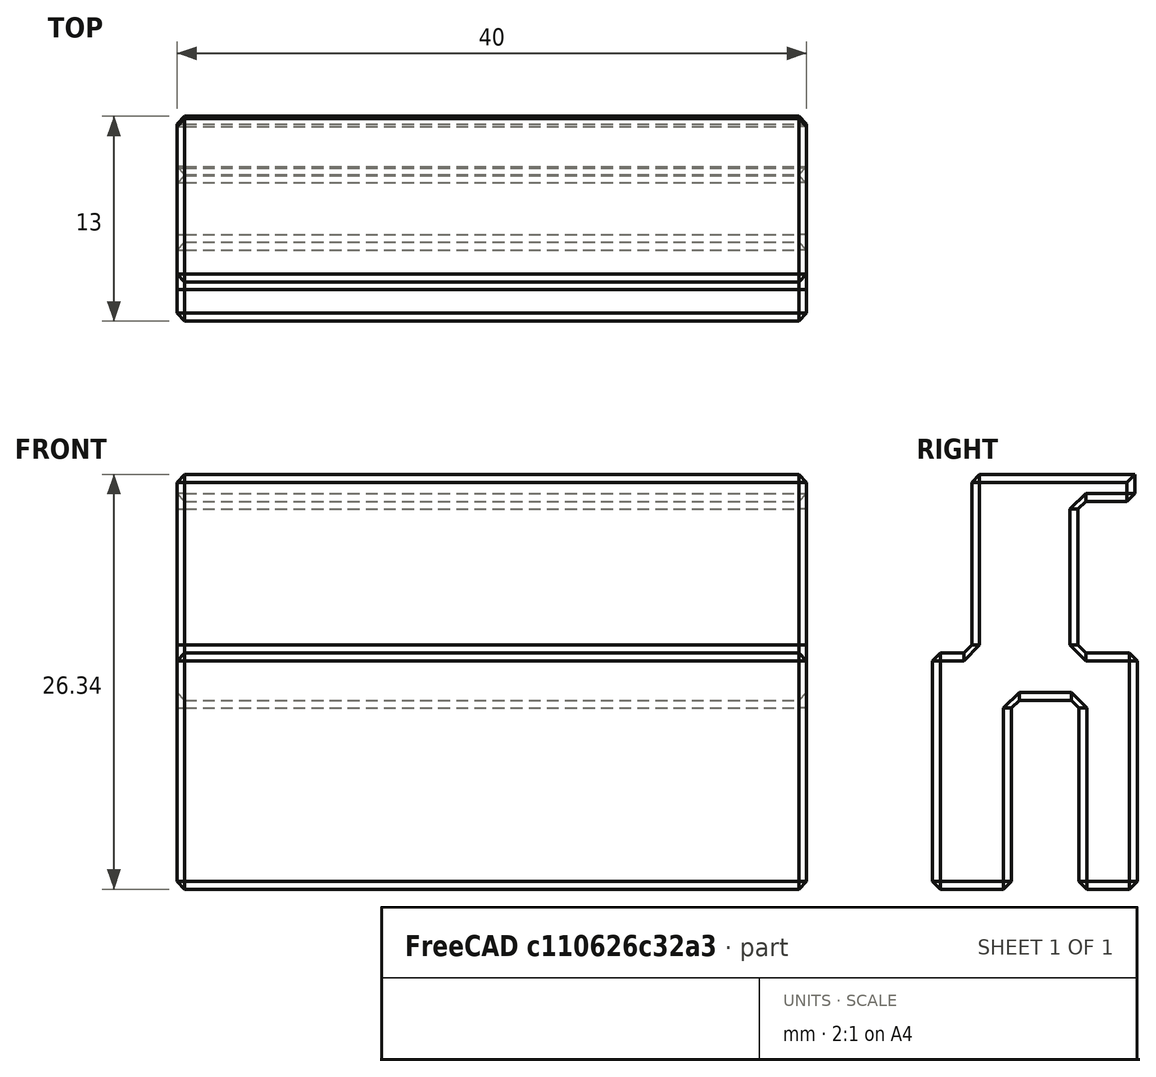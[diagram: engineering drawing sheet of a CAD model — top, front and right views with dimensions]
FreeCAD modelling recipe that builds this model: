
FCSTD DOCUMENT  (FreeCAD 0.21R)
Label: sensor_holder_adapter2
License: All rights reserved
LicenseURL: http://en.wikipedia.org/wiki/All_rights_reserved
objects: Sketcher::SketchObject×1, PartDesign::Pad×1, Mesh::Feature×1, PartDesign::Chamfer×1, PartDesign::Body×1
note: 6 computed .brp shape members not serialized (recipe doc carries the construction recipe); baked Part::Feature solids carry a one-line shape summary decoded from their .brp

FEATURE [Sketcher::SketchObject] Sketch005
  FullyConstrained = false
  MapMode = 5
  Placement = pos=(0,0,0) rot=(0.57735,0.57735,0.57735;2.0944rad)
  sketch-geometry (15):
    g0: LineSegment StartX=4.3 StartY=-10 StartZ=0 EndX=8 EndY=-10 EndZ=0
    g1: LineSegment StartX=8 StartY=-10 StartZ=0 EndX=8 EndY=5 EndZ=0
    g2: LineSegment StartX=4.3 StartY=2 StartZ=0 EndX=4.3 EndY=-10 EndZ=0
    g3: LineSegment StartX=0 StartY=2 StartZ=0 EndX=4.3 EndY=2 EndZ=0
    g4: LineSegment StartX=-5 StartY=5 StartZ=0 EndX=-2.51766 EndY=5 EndZ=0
    g5: LineSegment StartX=-5 StartY=5 StartZ=0 EndX=-5 EndY=-2.48828 EndZ=0
    g6: LineSegment StartX=-5 StartY=-2.48828 StartZ=0 EndX=-5 EndY=-10 EndZ=0
    g7: LineSegment StartX=-5 StartY=-10 StartZ=0 EndX=0 EndY=-10 EndZ=0
    g8: LineSegment StartX=0 StartY=-10 StartZ=0 EndX=0 EndY=2 EndZ=0
    g9: LineSegment StartX=7.84431 StartY=16.3375 StartZ=0 EndX=-2.51766 EndY=16.3375 EndZ=0
    g10: LineSegment StartX=4.22367 StartY=14.6399 StartZ=0 EndX=7.84431 EndY=14.6399 EndZ=0
    g11: LineSegment StartX=7.84431 StartY=14.6399 StartZ=0 EndX=7.84431 EndY=16.3375 EndZ=0
    g12: LineSegment StartX=4.22367 StartY=14.6399 StartZ=0 EndX=4.22367 EndY=5 EndZ=0
    g13: LineSegment StartX=-2.51766 StartY=5 StartZ=0 EndX=-2.51766 EndY=16.3375 EndZ=0
    g14: LineSegment StartX=4.22367 StartY=5 StartZ=0 EndX=8 EndY=5 EndZ=0
  constraints (37):
    c: Coincident(g0,g1)
    c: Coincident(g2,g0)
    c: Horizontal(g0)
    c: Vertical(g1)
    c: Vertical(g2)
    c: Horizontal(g3)
    c: Coincident(g2,g3)
    c: DistanceX(g3,g2) = 4.3
    c: DistanceY(g2,g2) = 12
    c: DistanceY(g1,g1) = 15
    c: Coincident(g14,g1)
    c: Horizontal(g4)
    c: DistanceX(g3,g0) = 8
    c: DistanceY(g-1,g4) = 5
    c: DistanceX(g-1,g3) = 0
    c: Coincident(g5,g4)
    c: DistanceX(g4) = -5
    c: Perpendicular(g4,g5)
    c: Coincident(g6,g5)
    c: Coincident(g7,g6)
    c: Coincident(g8,g7)
    c: Coincident(g8,g3)
    c: Perpendicular(g8,g3)
    c: Perpendicular(g8,g7)
    c: Perpendicular(g7,g6)
    c: DistanceY(g6,g-1) = 10
    c: Coincident(g10,g11)
    c: Coincident(g11,g9)
    c: Horizontal(g9)
    c: Horizontal(g10)
    c: Vertical(g11)
    c: Vertical(g12)
    c: Vertical(g13)
    c: Coincident(g14,g12)
    c: Coincident(g9,g13)
    c: Coincident(g10,g12)
    c: Perpendicular(g12,g14)
FEATURE [PartDesign::Pad] Pad
  Direction = (1,0,0)
  Length = 40
  Length2 = 10
  Placement = pos=(0,0,0) rot=(0.57735,0.57735,0.57735;2.0944rad)
  Profile = -> Sketch005
  ReferenceAxis = -> Sketch005 [N_Axis]
  Type = 0
FEATURE [Mesh::Feature] sensor_holder
  Placement = pos=(0,10,16.5) rot=(1,0,0;4.71239rad)
FEATURE [PartDesign::Chamfer] Chamfer
  Angle = 45
  Base = -> Pad [Face16,Face17,Face2,Face1,Face14,Edge5,Face3,Face7,Face8,Face10,Face11,Edge14,Edge11]
  BaseFeature = -> Pad
  ChamferType = 0
  FlipDirection = false
  Placement = pos=(0,0,0) rot=(0.57735,0.57735,0.57735;2.0944rad)
  Size = 0.5
  Size2 = 1
  SupportTransform = false
  UseAllEdges = false
FEATURE [PartDesign::Body] Body
  Group = -> [Sketch005,Pad,Chamfer]
  Origin = -> Origin
  Tip = -> Chamfer
